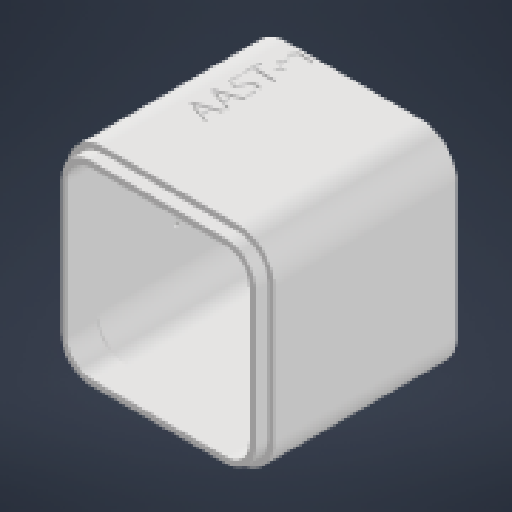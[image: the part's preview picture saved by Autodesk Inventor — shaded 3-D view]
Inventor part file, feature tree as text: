
AUTODESK INVENTOR PART (.ipt)
format: ipt  version: 2024 (Build 280153000, 153)  size: 673,792 bytes
history: native  units: mm
features: extrude x6, sketch x5, other x1, shell x1, chamfer x1
ambient origin geometry x8: Origin, YZ Plane, XZ Plane, XY Plane, X Axis, Y Axis, Z Axis, Center Point
bodies: Body1 (feature_tree), Body2 (feature_tree), Body3 (feature_tree), Body4 (feature_tree), Body5 (feature_tree), Body6 (feature_tree), Body7 (feature_tree)
feature tree (14):
  other  "솔리드1"
  extrude  "돌출1"  Depth=170.0mm
  shell  "쉘1"  Thickness=170.0mm
  sketch  "스케치2"
  extrude  "돌출2"  Depth=30.0mm
  chamfer  "모따기1"  Distance=30.0mm
  extrude  "돌출3"  Depth=30.0mm
  extrude  "돌출4"  Depth=150.0mm TaperAngle=0.0deg
  extrude  "돌출5"  Depth=5.0mm
  extrude  "돌출6"  Depth=170.0mm
  sketch  "스케치1"
  sketch  "스케치3"
  sketch  "스케치4"
  sketch  "스케치6"
